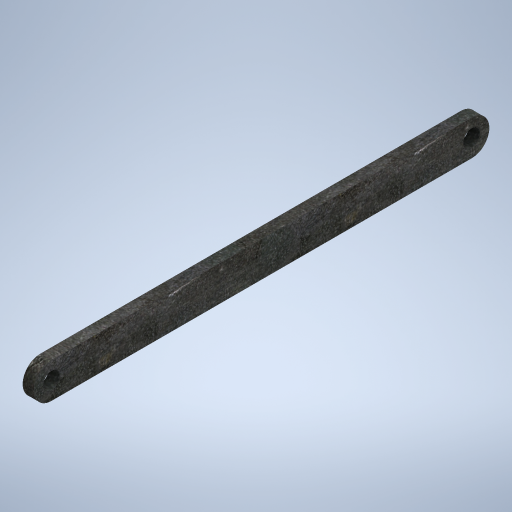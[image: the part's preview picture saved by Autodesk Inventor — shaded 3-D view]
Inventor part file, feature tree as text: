
AUTODESK INVENTOR PART (.ipt)
format: ipt  version: 2024 (Build 280153000, 153)  size: 353,280 bytes
history: native  units: mm
features: other x2, extrude x1, sketch x1
ambient origin geometry x8: Origin, YZ Plane, XZ Plane, XY Plane, X Axis, Y Axis, Z Axis, Center Point
bodies: Solid1 (feature_tree)
feature tree (4):
  extrude  "Extrusion1"  Depth=25.0mm
  other  "Full Round Fillet1"
  other  "Full Round Fillet2"
  sketch  "Sketch1"  dims[d0=325.0mm d1=25.0mm d2=12.5mm d3=162.5mm d4=12.0mm d5=12.5mm d6=12.0mm d7=12.5mm d8=8.0mm d9=0.0mm]
